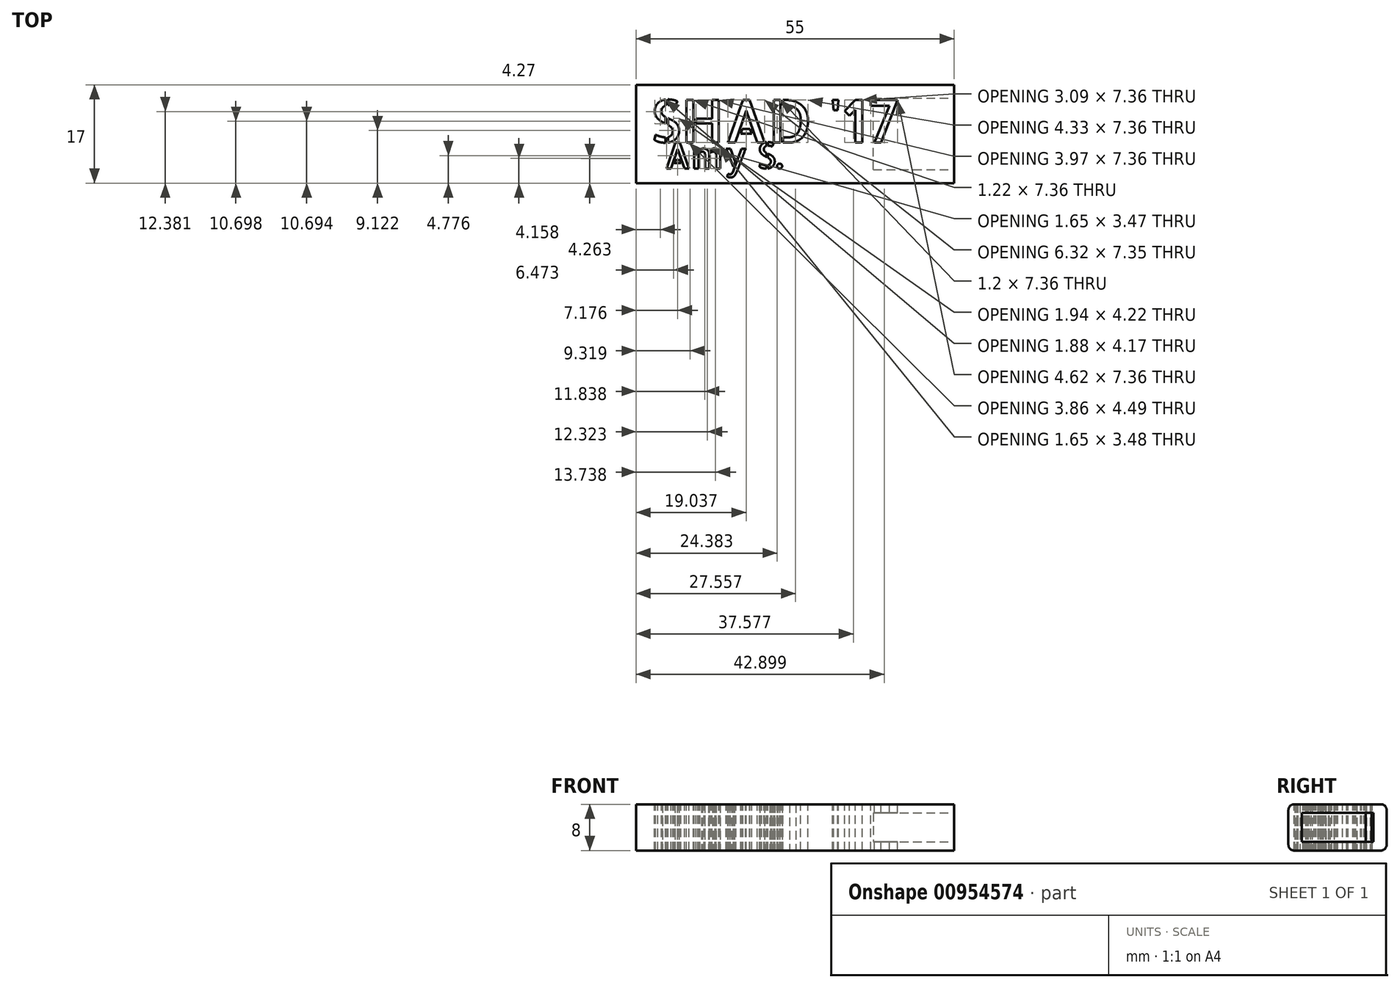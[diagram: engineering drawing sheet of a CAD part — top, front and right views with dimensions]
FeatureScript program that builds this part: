
annotation { "Feature Type Name" : "Feature", "Feature Type Description" : "" }
export const myFeature = defineFeature(function(context is Context, id is Id, definition is map)
    precondition{}
    {
        {
            var Q0;
            Q0=qCreatedBy(makeId("Front.planeOp"),FACE);
            var sketch = newSketch(context, id + "F0", { "sketchPlane" : qUnion([Q0])});
            skLineSegment(sketch, "E0.bottom", {"start": v(7.5, -4) * mm, "end": v(-7.5, -4) * mm});
            skLineSegment(sketch, "E0.top", {"start": v(7.5, 4) * mm, "end": v(-7.5, 4) * mm});
            skLineSegment(sketch, "E0.left", {"start": v(8.5, -3) * mm, "end": v(8.5, 3) * mm});
            skLineSegment(sketch, "E0.right", {"start": v(-8.5, -3) * mm, "end": v(-8.5, 3) * mm});
            skPoint(sketch, "E0.middle", {"position": v(0, 0) * mm});
            skPoint(sketch, "E1.visualSharp", {"position": v(-8.5, 4) * mm});
            skArc(sketch, "E1.filletArc", {"start": v(-7.5, 4) * mm, "mid": v(-8.2, 3.7) * mm, "end": v(-8.5, 3) * mm});
            skPoint(sketch, "E2.visualSharp", {"position": v(8.5, 4) * mm});
            skArc(sketch, "E2.filletArc", {"start": v(8.5, 3) * mm, "mid": v(8.2, 3.7) * mm, "end": v(7.5, 4) * mm});
            skPoint(sketch, "E3.visualSharp", {"position": v(8.5, -4) * mm});
            skArc(sketch, "E3.filletArc", {"start": v(7.5, -4) * mm, "mid": v(8.2, -3.7) * mm, "end": v(8.5, -3) * mm});
            skPoint(sketch, "E4.visualSharp", {"position": v(-8.5, -4) * mm});
            skArc(sketch, "E4.filletArc", {"start": v(-8.5, -3) * mm, "mid": v(-8.2, -3.7) * mm, "end": v(-7.5, -4) * mm});
            skSolve(sketch);
        }
        {
            var Q0;
            Q0 = qSketchRegion(id + "F0", true);
            extrude(context, id + "F1", {"entities" : qUnion([Q0]), "depth" : 55 * mm, "offsetDistance" : 25 * mm});
        }
        {
            var Q0;
            Q0=makeQuery(id+"F1.opExtrude","CAP_FACE",FACE,{"disambiguationData":[OSD([sQuery(id+"F0.wireOp",EDGE,"E0.bottom"),sQuery(id+"F0.wireOp",EDGE,"E0.top"),sQuery(id+"F0.wireOp",EDGE,"E0.left"),sQuery(id+"F0.wireOp",EDGE,"E0.right"),sQuery(id+"F0.wireOp",EDGE,"E1.filletArc"),sQuery(id+"F0.wireOp",EDGE,"E2.filletArc"),sQuery(id+"F0.wireOp",EDGE,"E3.filletArc"),sQuery(id+"F0.wireOp",EDGE,"E4.filletArc")])],"isStart":false});
            var sketch = newSketch(context, id + "F2", { "sketchPlane" : qUnion([Q0])});
            skLineSegment(sketch, "E5.bottom", {"start": v(-6.2, 2.5) * mm, "end": v(6.2, 2.5) * mm});
            skLineSegment(sketch, "E5.top", {"start": v(-6.2, -2.5) * mm, "end": v(6.2, -2.5) * mm});
            skLineSegment(sketch, "E5.left", {"start": v(-6.2, 2.5) * mm, "end": v(-6.2, -2.5) * mm});
            skLineSegment(sketch, "E5.right", {"start": v(6.2, 2.5) * mm, "end": v(6.2, -2.5) * mm});
            skPoint(sketch, "E5.middle", {"position": v(0, 0) * mm});
            skSolve(sketch);
        }
        {
            var Q0;
            Q0 = qSketchRegion(id + "F2", true);
            extrude(context, id + "F3", {"entities" : qUnion([Q0]), "operationType" : NewBodyOperationType.REMOVE, "oppositeDirection" : true, "depth" : 14 * mm, "offsetDistance" : 25 * mm});
        }
        {
            var Q0;
            Q0=makeQuery(id+"F1.opExtrude","SWEPT_BODY",BODY,{"disambiguationData":[OSD([sQuery(id+"F0.wireOp",EDGE,"E0.bottom"),sQuery(id+"F0.wireOp",EDGE,"E0.top"),sQuery(id+"F0.wireOp",EDGE,"E0.left"),sQuery(id+"F0.wireOp",EDGE,"E0.right"),sQuery(id+"F0.wireOp",EDGE,"E1.filletArc"),sQuery(id+"F0.wireOp",EDGE,"E2.filletArc"),sQuery(id+"F0.wireOp",EDGE,"E3.filletArc"),sQuery(id+"F0.wireOp",EDGE,"E4.filletArc")])]});
            var Q1;
            Q1=makeQuery(id+"F1.opExtrude","CAP_EDGE",EDGE,{"disambiguationData":[OSD([sQuery(id+"F0.wireOp",EDGE,"E0.right")])],"isStart":true});
            transform(context, id + "F4", {"entities" : qUnion([Q0]), "transformType" : TransformType.ROTATION, "transformAxis" : qUnion([Q1]), "angle" : 90 * degree, "makeCopy" : false});
        }
        {
            var Q0;
            Q0=makeQuery(id+"F1.opExtrude","SWEPT_FACE",FACE,{"disambiguationData":[OSD([sQuery(id+"F0.wireOp",EDGE,"E0.top")])]});
            var sketch = newSketch(context, id + "F5", { "sketchPlane" : qUnion([Q0])});
            skText(sketch, "E6", { "text": "SHAD \'17", "fontName": "AllertaStencil-Regular.ttf"});
            skText(sketch, "E7", { "text": "Amy S.", "fontName": "AllertaStencil-Regular.ttf"});
            const initialGuessF5  = {"E6": [-0.00614, 0.00702, 1, 0, 0.00736], "E7": [-0.00364, 0.00253, 1, 0, 0.0045]};
            skSetInitialGuess(sketch, initialGuessF5);
            skSolve(sketch);
        }
        {
            var Q0;
            Q0 = qSketchRegion(id + "F5", true);
            extrude(context, id + "F6", {"entities" : qUnion([Q0]), "operationType" : NewBodyOperationType.REMOVE, "oppositeDirection" : true, "depth" : 25 * mm, "offsetDistance" : 25 * mm});
        }
    });
